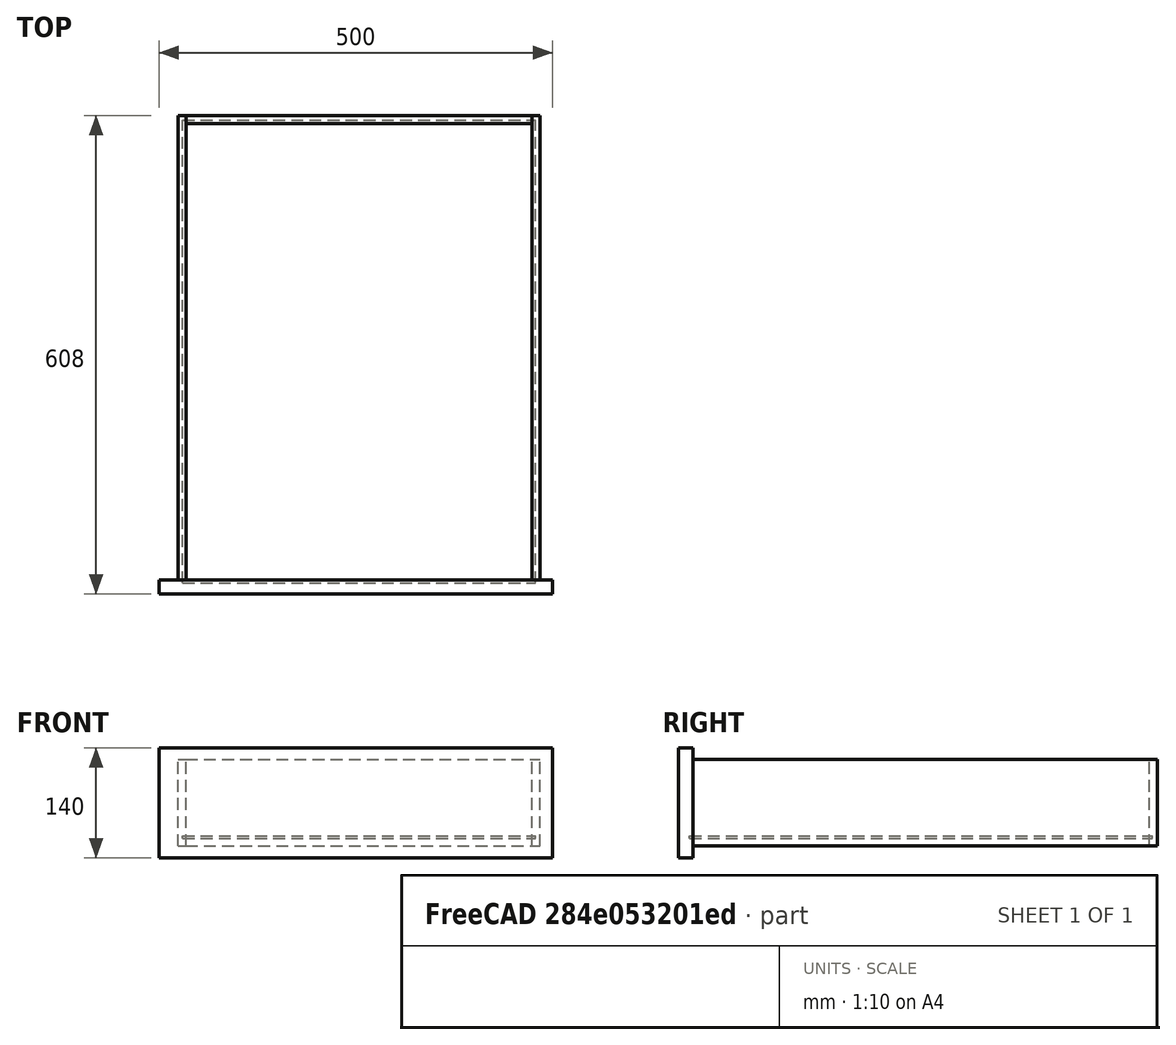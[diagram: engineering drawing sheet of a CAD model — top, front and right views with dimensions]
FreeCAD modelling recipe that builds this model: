
FCSTD DOCUMENT  (FreeCAD 1.1R20260325 (Git shallow))
Label: Drawer_001
License: All rights reserved
LicenseURL: http://en.wikipedia.org/wiki/All_rights_reserved
objects: Part::Box×5, App::LinkGroup×2, Spreadsheet::Sheet×1
note: 5 computed .brp shape members not serialized (recipe doc carries the construction recipe); baked Part::Feature solids carry a one-line shape summary decoded from their .brp

FEATURE [Spreadsheet::Sheet] Spreadsheet  label="settings"
  cells = A1='Drawer width; B1(dwidth)==460 mm; A2='Drawer depth; B2(ddepth)==590 mm; A3='Drawer height; B3(dheight)==110 mm; A4='Front width; B4(fwidth)==500 mm; A5='Front height; B5(fheight)==140 mm; A6='Drawer thickness; B6(dthick)==10 mm; A7='Front thickness; B7(fthick)==18 mm; A8='Bottom thickness; B8(bthick)==3 mm; A9='Bottom offset; B9(boffset)==10 mm; A10='Bottom sink; B10(bsink)==4 mm
FEATURE [Part::Box] Box  label="Bottom"
  AttacherType = Attacher::AttachEngine3D
  Height = 3
  Length = 448
  Placement = pos=(0,-4,10) rot=(0,0,1;0rad)
  Width = 588
  expr: .Placement.Base.y = -<<settings>>.bsink
  expr: .Placement.Base.z = <<settings>>.boffset
  expr: Height = <<settings>>.bthick
  expr: Length = <<settings>>.dwidth - 2 * <<settings>>.dthick + 2 * <<settings>>.bsink
  expr: Width = <<settings>>.ddepth - <<settings>>.dthick + 2 * <<settings>>.bsink
FEATURE [Part::Box] Box001  label="Left"
  AttacherType = Attacher::AttachEngine3D
  Height = 110
  Length = 10
  Placement = pos=(-6,0,0) rot=(0,0,1;0rad)
  Width = 590
  expr: .Placement.Base.x = -<<settings>>.dthick + <<settings>>.bsink
  expr: Height = <<settings>>.dheight
  expr: Length = <<settings>>.dthick
  expr: Width = <<settings>>.ddepth
FEATURE [Part::Box] Box002  label="Right"
  AttacherType = Attacher::AttachEngine3D
  Height = 110
  Length = 10
  Placement = pos=(444,0,0) rot=(0,0,1;0rad)
  Width = 590
  expr: .Placement.Base.x = <<settings>>.dwidth - 2 * <<settings>>.dthick + <<settings>>.bsink
  expr: Height = <<settings>>.dheight
  expr: Length = <<settings>>.dthick
  expr: Width = <<settings>>.ddepth
FEATURE [Part::Box] Box003  label="Back"
  AttacherType = Attacher::AttachEngine3D
  Height = 110
  Length = 440
  Placement = pos=(4,580,0) rot=(0,0,1;0rad)
  Width = 10
  expr: .Placement.Base.x = <<settings>>.bsink
  expr: .Placement.Base.y = <<settings>>.ddepth - <<settings>>.dthick
  expr: Height = <<settings>>.dheight
  expr: Length = <<settings>>.dwidth - 2 * <<settings>>.dthick
  expr: Width = <<settings>>.dthick
FEATURE [Part::Box] Box004  label="Front"
  AttacherType = Attacher::AttachEngine3D
  Height = 140
  Length = 500
  Placement = pos=(-30,-18,-15) rot=(0,0,1;0rad)
  Width = 18
  expr: .Placement.Base.x = -(<<settings>>.fwidth - <<settings>>.dwidth) / 2 - <<settings>>.dthick
  expr: .Placement.Base.y = -<<settings>>.fthick
  expr: .Placement.Base.z = -(<<settings>>.fheight - <<settings>>.dheight) / 2
  expr: Height = <<settings>>.fheight
  expr: Length = <<settings>>.fwidth
  expr: Width = <<settings>>.fthick
FEATURE [App::LinkGroup] LinkGroup  label="Drawer, link this"
  ElementList = -> [Box,Box001,Box002,Box003,Box004]
  LinkMode = 0
FEATURE [App::LinkGroup] LinkGroup001  label="Drawer, hide this"
  ElementList = -> [Spreadsheet,LinkGroup]
  LinkMode = 0
